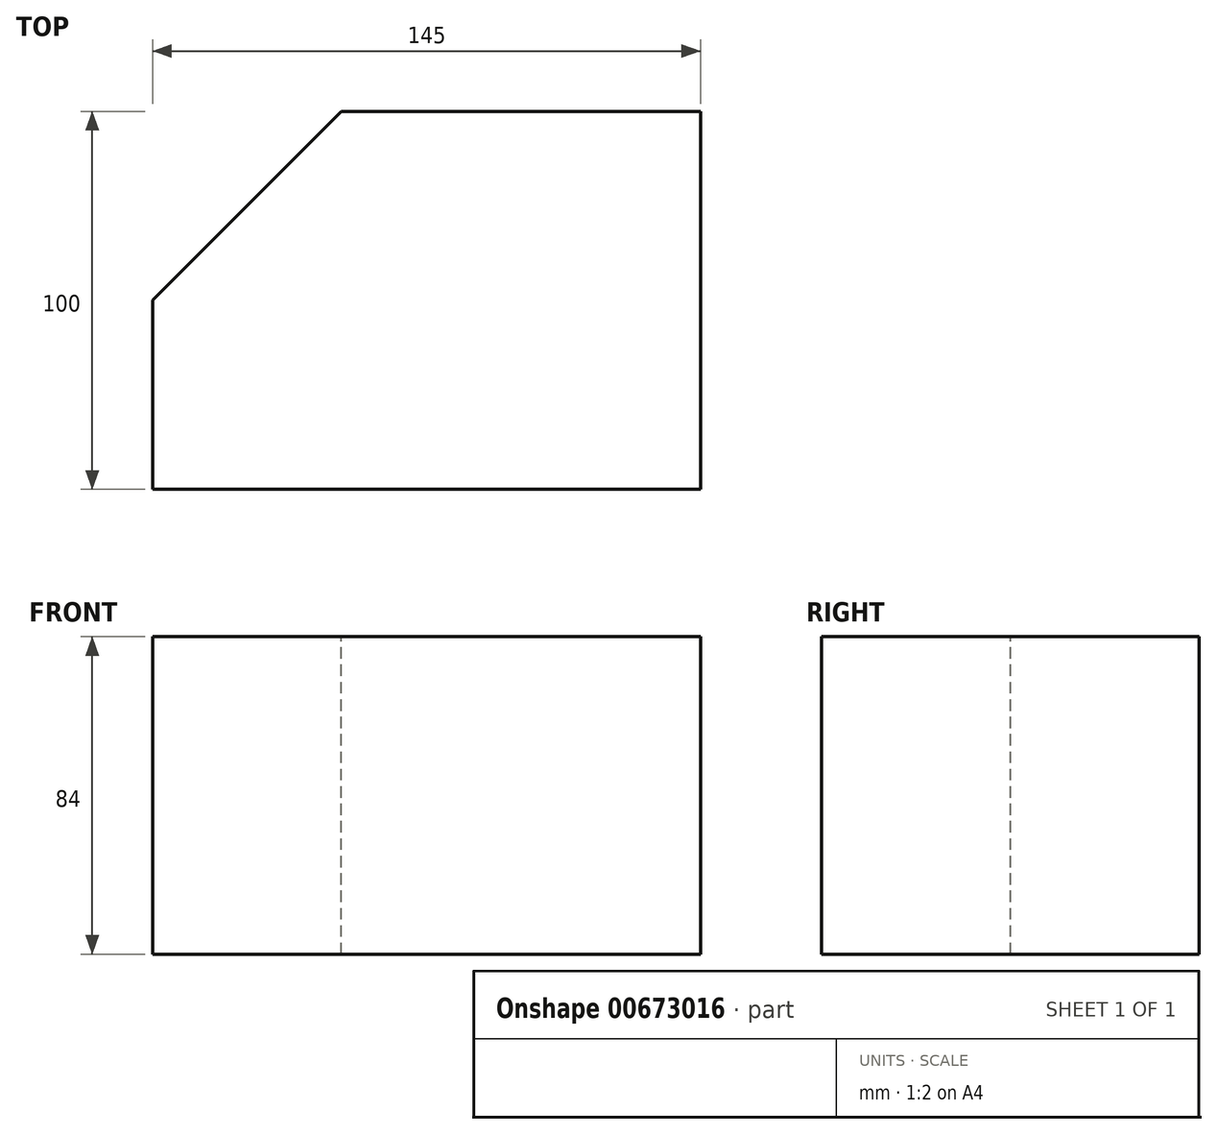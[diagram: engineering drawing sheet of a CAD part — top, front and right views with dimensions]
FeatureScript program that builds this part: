
annotation { "Feature Type Name" : "Feature", "Feature Type Description" : "" }
export const myFeature = defineFeature(function(context is Context, id is Id, definition is map)
    precondition{}
    {
        {
            var Q0;
            Q0=qCreatedBy(makeId("Front.planeOp"),FACE);
            var sketch = newSketch(context, id + "F0", { "sketchPlane" : qUnion([Q0])});
            skLineSegment(sketch, "E0.bottom", {"start": v(0, 0) * mm, "end": v(43.98, 0) * mm});
            skLineSegment(sketch, "E0.top", {"start": v(0, 38.98) * mm, "end": v(43.98, 38.98) * mm});
            skLineSegment(sketch, "E0.left", {"start": v(0, 0) * mm, "end": v(0, 38.98) * mm});
            skLineSegment(sketch, "E0.right", {"start": v(43.98, 0) * mm, "end": v(43.98, 38.98) * mm});
            skSolve(sketch);
        }
        {
            var Q0;
            Q0=makeQuery(id+"F0.imprint","IMPRINT",FACE,{"disambiguationData":[TD([[makeQuery(id+"F0.imprint","IMPRINT",EDGE,{"derivedFrom":sQuery(id+"F0.wireOp",EDGE,"E0.bottom")}),1.0]])]});
            extrude(context, id + "F1", {"entities" : qUnion([Q0]), "depth" : 145 * mm, "offsetDistance" : 25 * mm});
        }
        {
            var Q0;
            Q0=makeQuery(id+"F1.opExtrude","SWEPT_FACE",FACE,{"disambiguationData":[OSD([sQuery(id+"F0.wireOp",EDGE,"E0.left")])]});
            extrude(context, id + "F2", {"entities" : qUnion([Q0]), "operationType" : NewBodyOperationType.ADD, "oppositeDirection" : true, "depth" : 145 * mm, "offsetDistance" : 25 * mm});
        }
        {
            var Q0;
            {var subQ0=sQuery(id+"F0.wireOp",EDGE,"E0.bottom");Q0=makeQuery(id+"F2.boolean.opBoolean","MERGE",FACE,{"derivedFrom":[makeQuery(id+"F1.opExtrude","SWEPT_FACE",FACE,{"disambiguationData":[OSD([subQ0])]}),makeQuery(id+"F2.opExtrude","SWEPT_FACE",FACE,{"disambiguationData":[OSD([subQ0,sQuery(id+"F0.wireOp",EDGE,"E0.left")])]})]});}
            extrude(context, id + "F3", {"entities" : qUnion([Q0]), "operationType" : NewBodyOperationType.ADD, "oppositeDirection" : true, "depth" : 84 * mm, "offsetDistance" : 25 * mm});
        }
        {
            var Q0;
            Q0=makeQuery(id+"F3.opExtrude","CAP_FACE",FACE,{"disambiguationData":[OSD([sQuery(id+"F0.wireOp",EDGE,"E0.bottom"),sQuery(id+"F0.wireOp",EDGE,"E0.left")])],"isStart":false});
            var sketch = newSketch(context, id + "F4", { "sketchPlane" : qUnion([Q0])});
            skLineSegment(sketch, "E1.bottom", {"start": v(0, 0) * mm, "end": v(44.02, 0) * mm});
            skLineSegment(sketch, "E1.top", {"start": v(0, -37.36) * mm, "end": v(44.02, -37.36) * mm});
            skLineSegment(sketch, "E1.left", {"start": v(0, 0) * mm, "end": v(0, -37.36) * mm});
            skLineSegment(sketch, "E1.right", {"start": v(44.02, 0) * mm, "end": v(44.02, -37.36) * mm});
            skSolve(sketch);
        }
        {
            var Q0;
            Q0=makeQuery(id+"F4.imprint","IMPRINT",FACE,{"disambiguationData":[TD([[makeQuery(id+"F4.imprint","IMPRINT",EDGE,{"derivedFrom":sQuery(id+"F4.wireOp",EDGE,"E1.bottom")}),-1.0]])]});
            extrude(context, id + "F5", {"entities" : qUnion([Q0]), "depth" : 10 * mm, "offsetDistance" : 25 * mm});
        }
        {
            var Q0;
            Q0=makeQuery(id+"F5.opExtrude","SWEPT_FACE",FACE,{"disambiguationData":[OSD([sQuery(id+"F4.wireOp",EDGE,"E1.bottom")])]});
            extrude(context, id + "F6", {"entities" : qUnion([Q0]), "oppositeDirection" : true, "depth" : 50 * mm, "offsetDistance" : 25 * mm});
        }
        {
            var Q0;
            Q0=makeQuery(id+"F5.opExtrude","SWEPT_BODY",BODY,{"disambiguationData":[OSD([sQuery(id+"F4.wireOp",EDGE,"E1.bottom"),sQuery(id+"F4.wireOp",EDGE,"E1.top"),sQuery(id+"F4.wireOp",EDGE,"E1.left"),sQuery(id+"F4.wireOp",EDGE,"E1.right")])]});
            deleteBodies(context, id + "F7", {"entities" : qUnion([Q0])});
        }
        {
            var Q0;
            Q0=makeQuery(id+"F6.opExtrude","SWEPT_FACE",FACE,{"disambiguationData":[OSD([sQuery(id+"F4.wireOp",EDGE,"E1.bottom"),sQuery(id+"F4.wireOp",EDGE,"E1.left")])]});
            extrude(context, id + "F8", {"entities" : qUnion([Q0]), "oppositeDirection" : true, "depth" : 50 * mm, "offsetDistance" : 25 * mm});
        }
        {
            var Q0;
            Q0=makeQuery(id+"F6.opExtrude","SWEPT_BODY",BODY,{"disambiguationData":[OSD([sQuery(id+"F4.wireOp",EDGE,"E1.bottom")])]});
            deleteBodies(context, id + "F9", {"entities" : qUnion([Q0])});
        }
        {
            var Q0;
            Q0=makeQuery(id+"F3.opExtrude","CAP_FACE",FACE,{"disambiguationData":[OSD([sQuery(id+"F0.wireOp",EDGE,"E0.bottom"),sQuery(id+"F0.wireOp",EDGE,"E0.left")])],"isStart":false});
            var sketch = newSketch(context, id + "F10", { "sketchPlane" : qUnion([Q0])});
            skLineSegment(sketch, "E2", {"start": v(49.87, 0) * mm, "end": v(0, -49.9) * mm});
            skSolve(sketch);
        }
        {
            var Q0;
            {var subQ0=sQuery(id+"F10.wireOp",EDGE,"E2");Q0=makeQuery(id+"F10.imprint","IMPRINT",FACE,{"disambiguationData":[TD([[makeQuery(id+"F10.imprint","IMPRINT",EDGE,{"derivedFrom":subQ0}),-1.0]])]});}
            extrude(context, id + "F11", {"entities" : qUnion([Q0]), "operationType" : NewBodyOperationType.REMOVE, "oppositeDirection" : true, "depth" : 84 * mm, "offsetDistance" : 25 * mm});
        }
        {
            var Q0;
            Q0=makeQuery(id+"F8.opExtrude","SWEPT_BODY",BODY,{"disambiguationData":[OSD([sQuery(id+"F4.wireOp",EDGE,"E1.bottom"),sQuery(id+"F4.wireOp",EDGE,"E1.left")])]});
            deleteBodies(context, id + "F12", {"entities" : qUnion([Q0])});
        }
        {
            var Q0;
            {var subQ0=sQuery(id+"F0.wireOp",EDGE,"E0.left");var subQ1=sQuery(id+"F0.wireOp",EDGE,"E0.bottom");Q0=makeQuery(id+"F3.boolean.opBoolean","MERGE",FACE,{"derivedFrom":[makeQuery(id+"F2.boolean.opBoolean","MERGE",FACE,{"derivedFrom":[makeQuery(id+"F1.opExtrude","CAP_FACE",FACE,{"disambiguationData":[OSD([subQ1,sQuery(id+"F0.wireOp",EDGE,"E0.top"),subQ0,sQuery(id+"F0.wireOp",EDGE,"E0.right")])],"isStart":false}),makeQuery(id+"F2.opExtrude","SWEPT_FACE",FACE,{"disambiguationData":[OSD([subQ0]),TDD([makeQuery(id+"F1.opExtrude","CAP_EDGE",EDGE,{"disambiguationData":[OSD([subQ0])],"isStart":false})])]})]}),makeQuery(id+"F3.opExtrude","SWEPT_FACE",FACE,{"disambiguationData":[OSD([subQ1,subQ0]),TDD([makeQuery(id+"F2.boolean.opBoolean","MERGE",EDGE,{"derivedFrom":[makeQuery(id+"F1.opExtrude","CAP_EDGE",EDGE,{"disambiguationData":[OSD([subQ1])],"isStart":false}),makeQuery(id+"F2.opExtrude","SWEPT_EDGE",EDGE,{"disambiguationData":[OSD([subQ1,subQ0]),TDD([makeQuery(id+"F1.opExtrude","CAP_VERTEX",VERTEX,{"disambiguationData":[OSD([subQ1,subQ0])],"isStart":false})])]})]})])]})]});}
            extrude(context, id + "F13", {"entities" : qUnion([Q0]), "operationType" : NewBodyOperationType.REMOVE, "oppositeDirection" : true, "depth" : 45 * mm, "offsetDistance" : 25 * mm});
        }
    });
